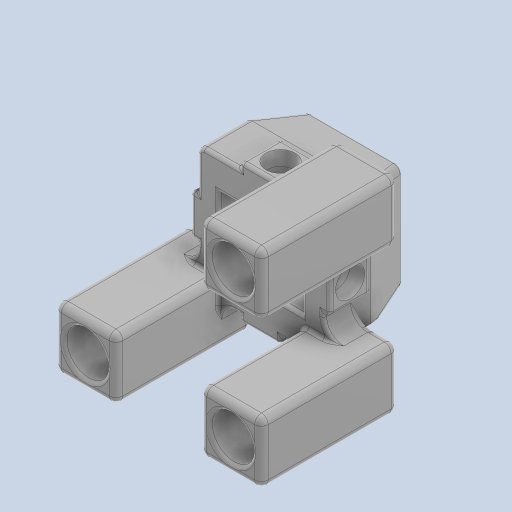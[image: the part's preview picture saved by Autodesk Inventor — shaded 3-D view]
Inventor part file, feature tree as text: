
AUTODESK INVENTOR PART (.ipt)
format: ipt  version: 2023 (Build 270158000, 158)  size: 1,797,632 bytes
history: native  units: mm
features: other x20, extrude x7, fillet x4, projected_geometry x2, chamfer x1, pattern_circular x1
ambient origin geometry x8: Origin, YZ Plane, XZ Plane, XY Plane, X Axis, Y Axis, Z Axis, Center Point
bodies: Solid1 (feature_tree)
feature tree (35):
  other  "Universal_ConstructorHead.ipt"
  other  "NP1_Docking.ipt"
  extrude  "Ex:Side1"  Depth=10.0mm TaperAngle=0.0deg
  other  "Sk:Side2"
  extrude  "Ex:RemoveExcess"  Depth=15.0mm TaperAngle=0.0deg
  extrude  "Ex:Side2"  Depth=15.0mm TaperAngle=0.0deg
  other  "Sk:PostHolder"
  extrude  "Ex:PostHolder"  Depth=15.0mm TaperAngle=0.0deg
  other  "TopCuffPlane"
  fillet  "Fillet:PostHolder1"  Radius=5.0mm
  fillet  "Fillet:PostHolder2"  Radius=10.0mm
  extrude  "Ex:PostHolderHole"  Depth=10.0mm
  other  "SideSketchPlane"
  other  "Sk:ThreadInsert"
  extrude  "Ex:ThreadHole"  Depth=4.0mm
  extrude  "Ex:ThreadInsert"  TaperAngle=0.0deg  [1 undecoded]
  fillet  "Fillet:ThreadInsert"  [1 undecoded]
  chamfer  "Chamfer:ThreadInsert"  Distance=0.8mm
  pattern_circular  "Pat:ThreadInsert"  [2 undecoded]
  fillet  "Filltet:Final"  Radius=1.15mm
  other  "Sk:Side1"
  other  "TaggingFeature2"
  other  "TaggingFeature4"
  other  "EndPlane_1"
  other  "AnglePlane2"
  other  "AnglePlane1_1"
  other  "FrontPlane"
  other  "SidePlane1"
  other  "SidePlane2"
  projected_geometry  "Projected Loop2"
  projected_geometry  "Projected Loop3"
  other  "Solid1::Universal_ConstructorHead.ipt"
  other  "Srf2"
  other  "Solid1::NP1_Docking.ipt"
  other  "Srf3"
note: 4 required parameter values undecoded (feature->parameter linkage not recoverable at this tier; creation-order binding heuristic only, values carry confidence <= 0.55)
